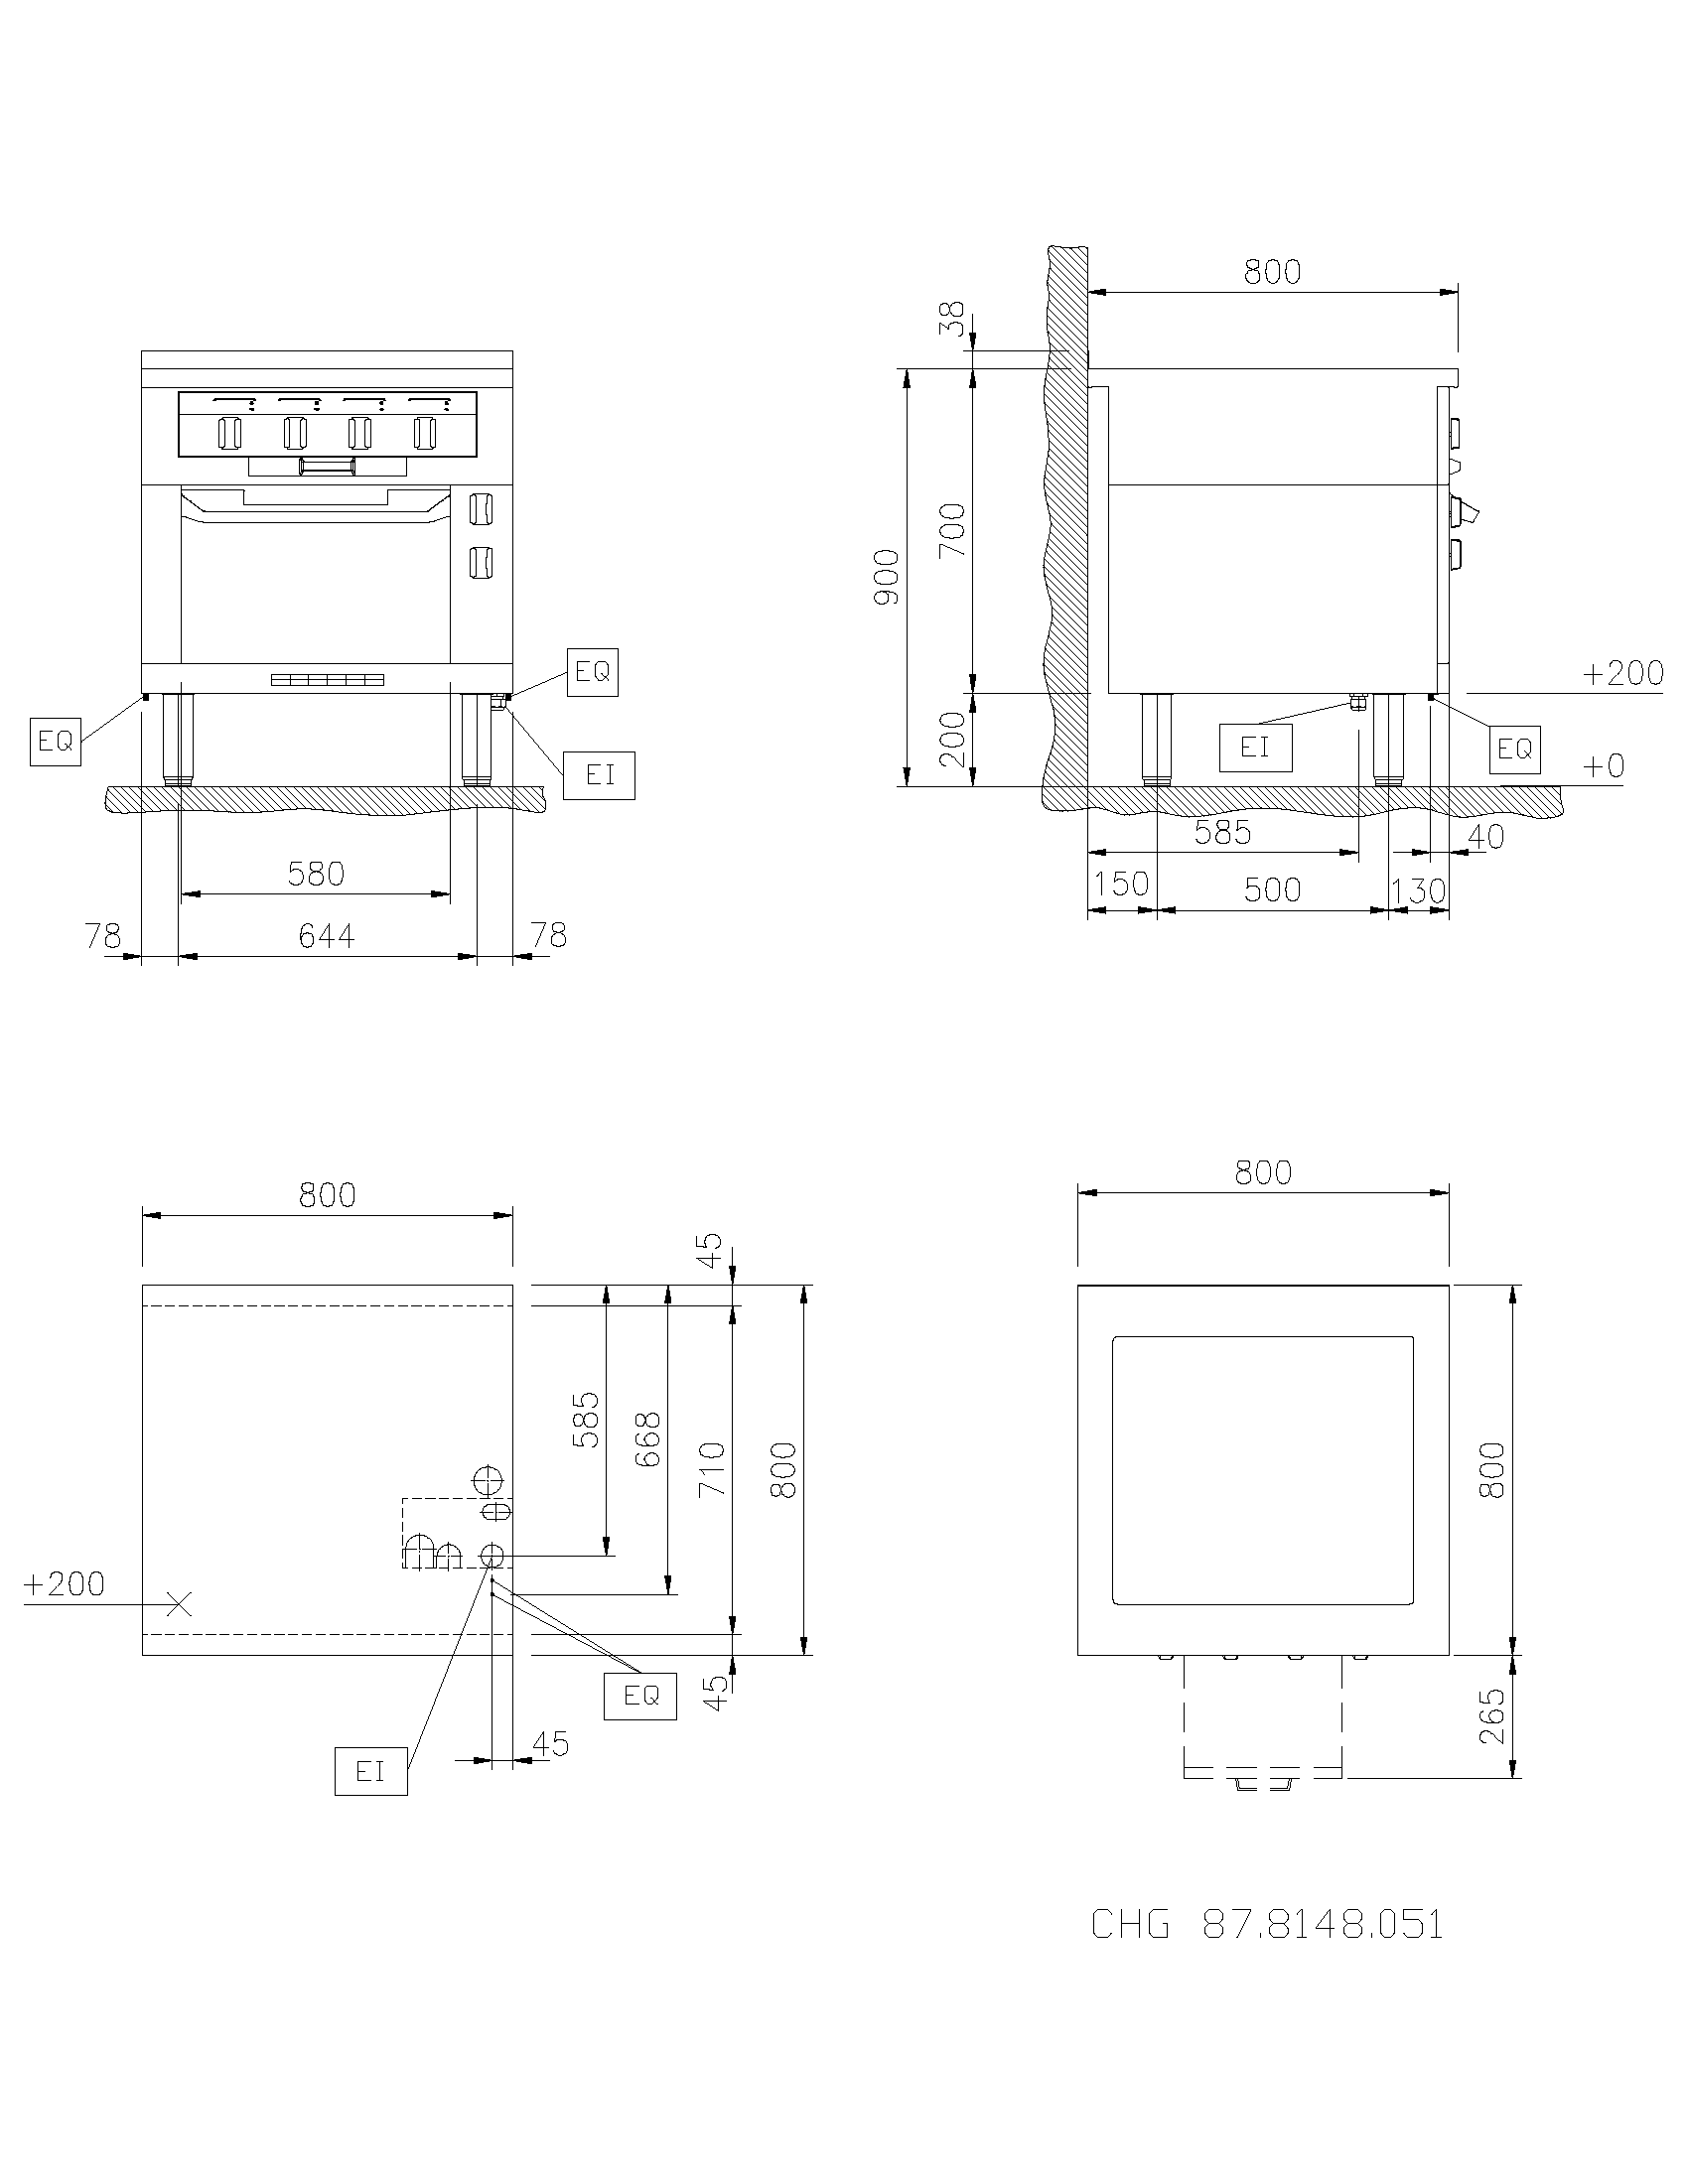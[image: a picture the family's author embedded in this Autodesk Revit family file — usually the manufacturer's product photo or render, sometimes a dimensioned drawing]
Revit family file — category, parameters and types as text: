
# Revit family: QF_ELECTROLUXPROFESSIONAL_588422_MALOFCH8AO
name_source: partatom
category: Attrezzature speciali
units: mm (PartAtom-declared; Revit-internal decimal feet)

## family parameters
Basato su piano di lavoro = No
Condiviso = No
Punto di calcolo locali = No
Quota connettore circolare = Usa diametro
Sempre verticale = Sì
Taglio con vuoti quando caricato = No
Tipo di parte = Normale

## types (1)
- Standard
    Accessory = Sì
    Cold Water Size = 0"
    Compressed Air Pressure = 0.00 psi
    Compressed Air Size = 0"
    Compressed Air Volume = 0 GPM
    Condensate Return Size = 0"
    Cycle = 50 Hz
    Depth Actual = 800 mm  [stored 2.62467 ft]
    Descrizione = EL.SOLID T,ECO,ST.OV,PASS,2S,800X800X800
    Direct Waste Size = 0"
    Gas Input Pressure = 0.0
    Gas KW = 0
    Gas Size = 0"
    HP = 23.2 HP
    Height Actual = 800 mm  [stored 2.62467 ft]
    Hot Water Size = 0"
    Item Number = 588422
    Length Actual = 800 mm  [stored 2.62467 ft]
    Modello = MALOFCH8AO
    Phase = 3
    Produttore = Electrolux Professional
    Prospetto di default = 0 mm  [stored 0 ft]
    Refrigerant Compressor Remote = Sì
    Refrigeration Liquid Line Size = 0 mm  [stored 0 ft]
    Refrigeration Suction Line Size = 0 mm  [stored 0 ft]
    Steam Consumption per Hour = 0
    Steam Supply Maximum Pressure = 0.00 psi
    Steam Supply Minimum Pressure = 0.00 psi
    Steam Supply Size = 0"
    URL = https://www.electroluxprofessional.com
    URL Manufacturer = https://www.electroluxprofessional.com
    Volts = 400 V
    Watts = 17300 W
    Weight = 211.00 kg

note: source unit labels omitted for Gas Input Pressure — the stored unit's dimension contradicts the parameter name (converter mislabeling)

note: [stored X ft] marks values corroborated as IEEE doubles in the binary element streams (Revit-internal decimal feet)

## geometry (parser evidence)
native form markers: Blend x24, Sweep x15
no freeform markers — native parametric forms only
